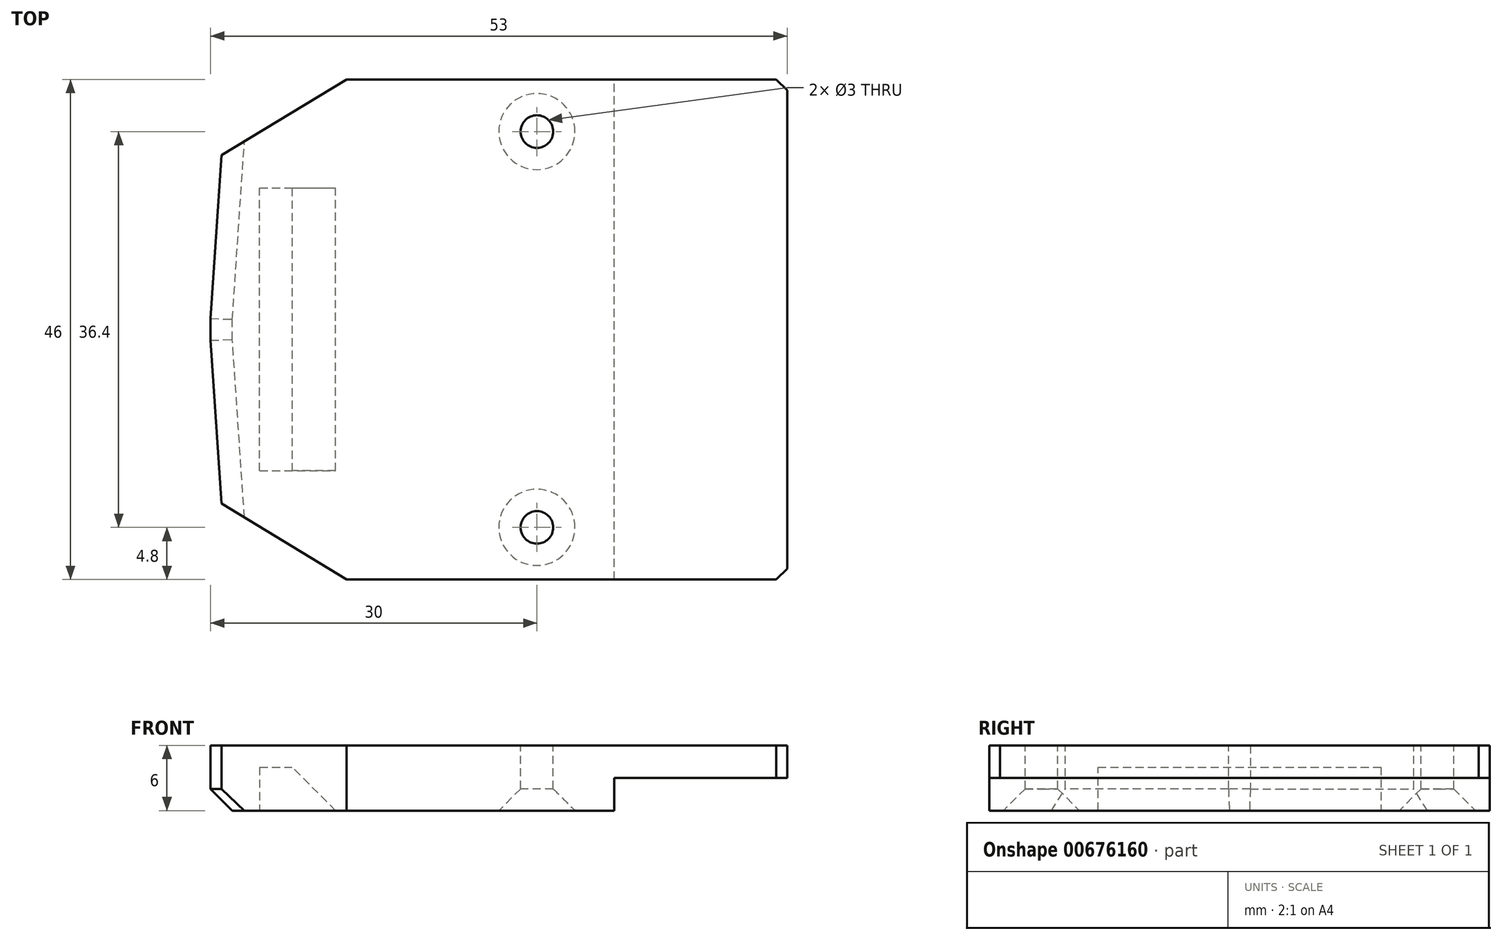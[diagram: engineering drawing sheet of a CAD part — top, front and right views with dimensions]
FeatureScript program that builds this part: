
annotation { "Feature Type Name" : "Feature", "Feature Type Description" : "" }
export const myFeature = defineFeature(function(context is Context, id is Id, definition is map)
    precondition{}
    {
        {
            var Q0;
            Q0=qCreatedBy(makeId("Front.planeOp"),FACE);
            var sketch = newSketch(context, id + "F0", { "sketchPlane" : qUnion([Q0])});
            skLineSegment(sketch, "E0", {"start": v(0, 0) * mm, "end": v(0, 3) * mm});
            skLineSegment(sketch, "E1", {"start": v(0, 3) * mm, "end": v(-53, 3) * mm});
            skLineSegment(sketch, "E2", {"start": v(-53, 3) * mm, "end": v(-53, -3) * mm});
            skLineSegment(sketch, "E3", {"start": v(-53, -3) * mm, "end": v(-15.9, -3) * mm});
            skLineSegment(sketch, "E4", {"start": v(-15.9, -3) * mm, "end": v(-15.9, 0) * mm});
            skLineSegment(sketch, "E5", {"start": v(-15.9, 0) * mm, "end": v(0, 0) * mm});
            skSolve(sketch);
        }
        {
            var Q0;
            Q0=makeQuery(id+"F0.imprint","IMPRINT",FACE,{"disambiguationData":[TD([[makeQuery(id+"F0.imprint","IMPRINT",EDGE,{"derivedFrom":sQuery(id+"F0.wireOp",EDGE,"E0")}),1.0]])]});
            extrude(context, id + "F1", {"entities" : qUnion([Q0]), "depth" : 46 * mm, "offsetDistance" : 25 * mm});
        }
        {
            var Q0;
            Q0=makeQuery(id+"F1.opExtrude","SWEPT_FACE",FACE,{"disambiguationData":[OSD([sQuery(id+"F0.wireOp",EDGE,"E1")])]});
            var sketch = newSketch(context, id + "F2", { "sketchPlane" : qUnion([Q0])});
            skCircle(sketch, "E6", {"center": v(-23, -4.8) * mm, "radius": 1.5 * mm});
            skCircle(sketch, "E7", {"center": v(-23, -41.2) * mm, "radius": 1.5 * mm});
            skLineSegment(sketch, "E8", {"start": v(-23, -4.8) * mm, "end": v(-23, 0) * mm, "construction": true});
            skLineSegment(sketch, "E9", {"start": v(-23, -41.2) * mm, "end": v(-23, -46) * mm, "construction": true});
            skSolve(sketch);
        }
        {
            var Q0;
            Q0=makeQuery(id+"F2.imprint","IMPRINT",FACE,{"disambiguationData":[TD([[makeQuery(id+"F2.imprint","IMPRINT",EDGE,{"derivedFrom":sQuery(id+"F2.wireOp",EDGE,"E6")}),1.0]])]});
            var Q1;
            Q1=makeQuery(id+"F2.imprint","IMPRINT",FACE,{"disambiguationData":[TD([[makeQuery(id+"F2.imprint","IMPRINT",EDGE,{"derivedFrom":sQuery(id+"F2.wireOp",EDGE,"E7")}),1.0]])]});
            extrude(context, id + "F3", {"entities" : qUnion([Q0, Q1]), "operationType" : NewBodyOperationType.REMOVE, "oppositeDirection" : true, "depth" : 25 * mm, "offsetDistance" : 25 * mm});
        }
        {
            var Q0;
            Q0=makeQuery(id+"F1.opExtrude","CAP_EDGE",EDGE,{"disambiguationData":[OSD([sQuery(id+"F0.wireOp",EDGE,"E2")])],"isStart":true});
            var Q1;
            Q1=makeQuery(id+"F1.opExtrude","CAP_EDGE",EDGE,{"disambiguationData":[OSD([sQuery(id+"F0.wireOp",EDGE,"E2")])],"isStart":false});
            chamfer(context, id + "F4", {"entities" : qUnion([Q0, Q1]), "chamferType" : ChamferType.TWO_OFFSETS, "width1" : 22 * mm, "oppositeDirection" : false, "width2" : 1.5 * mm, "tangentPropagation" : true});
        }
        {
            var Q0;
            {var subQ0=sQuery(id+"F0.wireOp",EDGE,"E2");Q0=makeQuery(id+"F4.opChamfer","BLEND_EDGE",EDGE,{"blendedFrom":[makeQuery(id+"F1.opExtrude","CAP_EDGE",EDGE,{"disambiguationData":[OSD([subQ0])],"isStart":true}),makeQuery(id+"F1.opExtrude","CAP_FACE",FACE,{"disambiguationData":[OSD([sQuery(id+"F0.wireOp",EDGE,"E0"),sQuery(id+"F0.wireOp",EDGE,"E1"),subQ0,sQuery(id+"F0.wireOp",EDGE,"E3"),sQuery(id+"F0.wireOp",EDGE,"E4"),sQuery(id+"F0.wireOp",EDGE,"E5")])],"isStart":true})],"blendedInto":[makeQuery(id+"F1.opExtrude","CAP_FACE",FACE,{"disambiguationData":[OSD([sQuery(id+"F0.wireOp",EDGE,"E0"),sQuery(id+"F0.wireOp",EDGE,"E1"),subQ0,sQuery(id+"F0.wireOp",EDGE,"E3"),sQuery(id+"F0.wireOp",EDGE,"E4"),sQuery(id+"F0.wireOp",EDGE,"E5")])],"isStart":true})]});}
            var Q1;
            {var subQ0=sQuery(id+"F0.wireOp",EDGE,"E2");Q1=makeQuery(id+"F4.opChamfer","BLEND_EDGE",EDGE,{"blendedFrom":[makeQuery(id+"F1.opExtrude","CAP_EDGE",EDGE,{"disambiguationData":[OSD([subQ0])],"isStart":false}),makeQuery(id+"F1.opExtrude","CAP_FACE",FACE,{"disambiguationData":[OSD([sQuery(id+"F0.wireOp",EDGE,"E0"),sQuery(id+"F0.wireOp",EDGE,"E1"),subQ0,sQuery(id+"F0.wireOp",EDGE,"E3"),sQuery(id+"F0.wireOp",EDGE,"E4"),sQuery(id+"F0.wireOp",EDGE,"E5")])],"isStart":false})],"blendedInto":[makeQuery(id+"F1.opExtrude","CAP_FACE",FACE,{"disambiguationData":[OSD([sQuery(id+"F0.wireOp",EDGE,"E0"),sQuery(id+"F0.wireOp",EDGE,"E1"),subQ0,sQuery(id+"F0.wireOp",EDGE,"E3"),sQuery(id+"F0.wireOp",EDGE,"E4"),sQuery(id+"F0.wireOp",EDGE,"E5")])],"isStart":false})]});}
            chamfer(context, id + "F5", {"entities" : qUnion([Q0, Q1]), "chamferType" : ChamferType.TWO_OFFSETS, "width1" : 11 * mm, "oppositeDirection" : false, "width2" : 7 * mm, "tangentPropagation" : true});
        }
        {
            var Q0;
            Q0=qCreatedBy(makeId("Front.planeOp"),FACE);
            cPlane(context, id + "F6", {"entities" : qUnion([Q0]), "cplaneType" : CPlaneType.OFFSET, "offset" : 23 * mm, "width" : 150 * mm, "height" : 150 * mm});
        }
        {
            var Q0;
            Q0=makeQuery(id+"F1.opExtrude","SWEPT_FACE",FACE,{"disambiguationData":[OSD([sQuery(id+"F0.wireOp",EDGE,"E3")])]});
            var sketch = newSketch(context, id + "F7", { "sketchPlane" : qUnion([Q0])});
            skLineSegment(sketch, "E10.bottom", {"start": v(-48.5, 36) * mm, "end": v(-41.5, 36) * mm});
            skLineSegment(sketch, "E10.top", {"start": v(-48.5, 10) * mm, "end": v(-41.5, 10) * mm});
            skLineSegment(sketch, "E10.left", {"start": v(-48.5, 36) * mm, "end": v(-48.5, 10) * mm});
            skLineSegment(sketch, "E10.right", {"start": v(-41.5, 36) * mm, "end": v(-41.5, 10) * mm});
            skSolve(sketch);
        }
        {
            var Q0;
            Q0=makeQuery(id+"F7.imprint","IMPRINT",FACE,{"disambiguationData":[TD([[makeQuery(id+"F7.imprint","IMPRINT",EDGE,{"derivedFrom":sQuery(id+"F7.wireOp",EDGE,"E10.bottom")}),-1.0]])]});
            extrude(context, id + "F8", {"entities" : qUnion([Q0]), "operationType" : NewBodyOperationType.REMOVE, "oppositeDirection" : true, "depth" : 4 * mm, "offsetDistance" : 25 * mm});
        }
        {
            var Q0;
            Q0=makeQuery(id+"F8.boolean.opBoolean","COPY",EDGE,{"derivedFrom":makeQuery(id+"F8.opExtrude","CAP_EDGE",EDGE,{"disambiguationData":[OSD([sQuery(id+"F7.wireOp",EDGE,"E10.right")])],"isStart":false})});
            chamfer(context, id + "F9", {"entities" : qUnion([Q0]), "width" : 4 * mm, "tangentPropagation" : true});
        }
        {
            var Q0;
            Q0=makeQuery(id+"F4.opChamfer","BLEND_EDGE",EDGE,{"blendedFrom":[makeQuery(id+"F1.opExtrude","CAP_EDGE",EDGE,{"disambiguationData":[OSD([sQuery(id+"F0.wireOp",EDGE,"E2")])],"isStart":false}),makeQuery(id+"F1.opExtrude","SWEPT_FACE",FACE,{"disambiguationData":[OSD([sQuery(id+"F0.wireOp",EDGE,"E3")])]})],"blendedInto":[makeQuery(id+"F1.opExtrude","SWEPT_FACE",FACE,{"disambiguationData":[OSD([sQuery(id+"F0.wireOp",EDGE,"E3")])]})]});
            var Q1;
            Q1=makeQuery(id+"F1.opExtrude","SWEPT_EDGE",EDGE,{"disambiguationData":[OSD([sQuery(id+"F0.wireOp",EDGE,"E2"),sQuery(id+"F0.wireOp",EDGE,"E3")])]});
            var Q2;
            Q2=makeQuery(id+"F4.opChamfer","BLEND_EDGE",EDGE,{"blendedFrom":[makeQuery(id+"F1.opExtrude","CAP_EDGE",EDGE,{"disambiguationData":[OSD([sQuery(id+"F0.wireOp",EDGE,"E2")])],"isStart":true}),makeQuery(id+"F1.opExtrude","SWEPT_FACE",FACE,{"disambiguationData":[OSD([sQuery(id+"F0.wireOp",EDGE,"E3")])]})],"blendedInto":[makeQuery(id+"F1.opExtrude","SWEPT_FACE",FACE,{"disambiguationData":[OSD([sQuery(id+"F0.wireOp",EDGE,"E3")])]})]});
            chamfer(context, id + "F10", {"entities" : qUnion([Q0, Q1, Q2]), "width" : 2 * mm, "tangentPropagation" : true});
        }
        {
            var Q0;
            Q0=makeQuery(id+"F1.opExtrude","CAP_EDGE",EDGE,{"disambiguationData":[OSD([sQuery(id+"F0.wireOp",EDGE,"E0")])],"isStart":true});
            var Q1;
            Q1=makeQuery(id+"F1.opExtrude","CAP_EDGE",EDGE,{"disambiguationData":[OSD([sQuery(id+"F0.wireOp",EDGE,"E0")])],"isStart":false});
            chamfer(context, id + "F11", {"entities" : qUnion([Q0, Q1]), "width" : 1 * mm, "tangentPropagation" : true});
        }
        {
            var Q0;
            Q0=makeQuery(id+"F3.boolean.opBoolean","INTERSECT",EDGE,{"derivedFrom":[makeQuery(id+"F1.opExtrude","SWEPT_FACE",FACE,{"disambiguationData":[OSD([sQuery(id+"F0.wireOp",EDGE,"E3")])]}),makeQuery(id+"F3.opExtrude","SWEPT_FACE",FACE,{"disambiguationData":[OSD([sQuery(id+"F2.wireOp",EDGE,"E7")])]})]});
            var Q1;
            Q1=makeQuery(id+"F3.boolean.opBoolean","INTERSECT",EDGE,{"derivedFrom":[makeQuery(id+"F1.opExtrude","SWEPT_FACE",FACE,{"disambiguationData":[OSD([sQuery(id+"F0.wireOp",EDGE,"E3")])]}),makeQuery(id+"F3.opExtrude","SWEPT_FACE",FACE,{"disambiguationData":[OSD([sQuery(id+"F2.wireOp",EDGE,"E6")])]})]});
            chamfer(context, id + "F12", {"entities" : qUnion([Q0, Q1]), "width" : 2 * mm, "tangentPropagation" : true});
        }
    });
